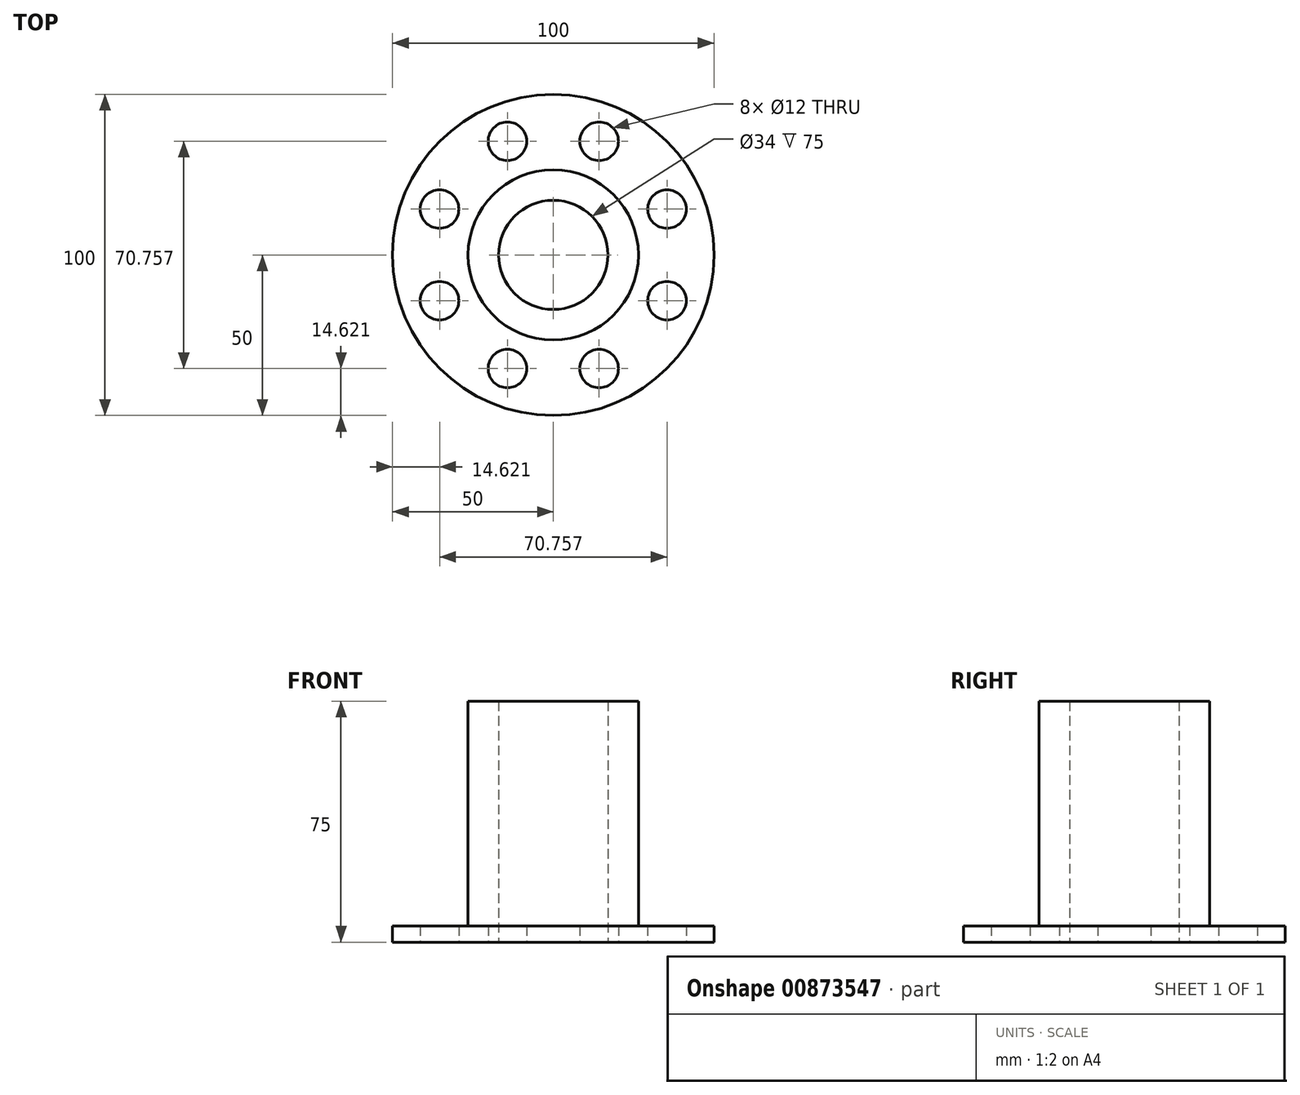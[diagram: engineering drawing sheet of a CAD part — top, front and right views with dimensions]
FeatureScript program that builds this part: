
annotation { "Feature Type Name" : "Feature", "Feature Type Description" : "" }
export const myFeature = defineFeature(function(context is Context, id is Id, definition is map)
    precondition{}
    {
        {
            var Q0;
            Q0=qCreatedBy(makeId("Top.planeOp"),FACE);
            var sketch = newSketch(context, id + "F0", { "sketchPlane" : qUnion([Q0])});
            skCircle(sketch, "E0", {"center": v(0, 0) * mm, "radius": 26.5 * mm});
            skCircle(sketch, "E1", {"center": v(0, 0) * mm, "radius": 50 * mm});
            skCircle(sketch, "E2", {"center": v(0, 0) * mm, "radius": 17 * mm});
            skCircle(sketch, "E3", {"center": v(0, 0) * mm, "radius": 34.48 * mm, "construction": true});
            skCircle(sketch, "E4", {"center": v(0, 0) * mm, "radius": 42.57 * mm, "construction": true});
            skCircle(sketch, "E5", {"center": v(14.27, 35.38) * mm, "radius": 6 * mm});
            skCircle(sketch, "E6.MirrorC", {"center": v(-14.27, 35.38) * mm, "radius": 6 * mm});
            skCircle(sketch, "E7.MirrorC", {"center": v(-35.38, 14.27) * mm, "radius": 6 * mm});
            skCircle(sketch, "E8.MirrorC", {"center": v(35.38, 14.27) * mm, "radius": 6 * mm});
            skCircle(sketch, "E9.MirrorC", {"center": v(-35.38, -14.27) * mm, "radius": 6 * mm});
            skCircle(sketch, "E10.MirrorC", {"center": v(-14.27, -35.38) * mm, "radius": 6 * mm});
            skCircle(sketch, "E11.MirrorC", {"center": v(35.38, -14.27) * mm, "radius": 6 * mm});
            skCircle(sketch, "E12.MirrorC", {"center": v(14.27, -35.38) * mm, "radius": 6 * mm});
            skSolve(sketch);
        }
        {
            var Q0;
            Q0=makeQuery(id+"F0.imprint","IMPRINT",FACE,{"disambiguationData":[TD([[makeQuery(id+"F0.imprint","IMPRINT",EDGE,{"derivedFrom":sQuery(id+"F0.wireOp",EDGE,"E0")}),-1.0]])]});
            var Q1;
            Q1=sQuery(id+"F0.wireOp",EDGE,"E1");
            extrude(context, id + "F1", {"entities" : qUnion([Q0]), "flatOperationType" : FlatOperationType.REMOVE, "surfaceEntities" : qUnion([Q1]), "depth" : 5 * mm, "offsetDistance" : 25 * mm, "domain" : OperationDomain.MODEL});
        }
        {
            var Q0;
            Q0=makeQuery(id+"F0.imprint","IMPRINT",FACE,{"disambiguationData":[TD([[makeQuery(id+"F0.imprint","IMPRINT",EDGE,{"derivedFrom":sQuery(id+"F0.wireOp",EDGE,"E0")}),1.0]])]});
            extrude(context, id + "F2", {"entities" : qUnion([Q0]), "operationType" : NewBodyOperationType.ADD, "flatOperationType" : FlatOperationType.REMOVE, "depth" : 75 * mm, "offsetDistance" : 25 * mm, "domain" : OperationDomain.MODEL});
        }
    });
